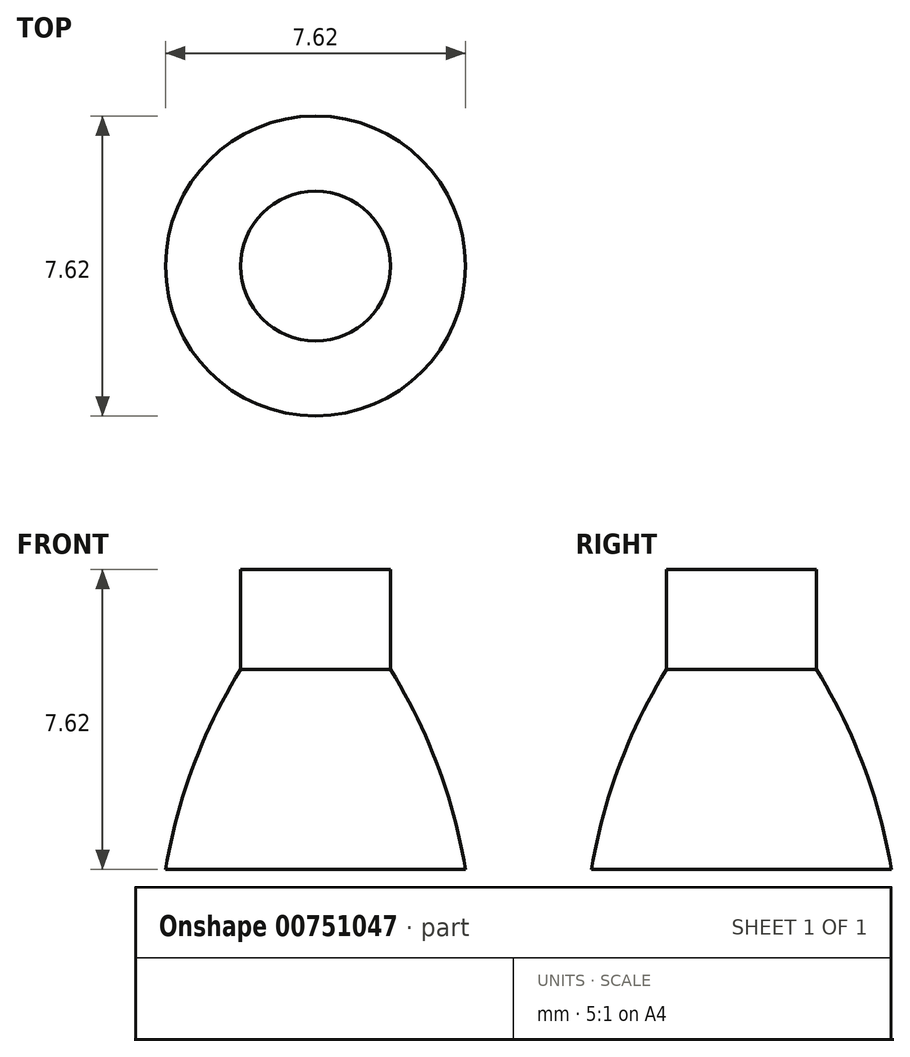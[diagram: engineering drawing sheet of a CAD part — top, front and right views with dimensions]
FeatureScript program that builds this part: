
annotation { "Feature Type Name" : "Feature", "Feature Type Description" : "" }
export const myFeature = defineFeature(function(context is Context, id is Id, definition is map)
    precondition{}
    {
        {
            var Q0;
            Q0=qCreatedBy(makeId("Front.planeOp"),FACE);
            var sketch = newSketch(context, id + "F0", { "sketchPlane" : qUnion([Q0])});
            skLineSegment(sketch, "E0", {"start": v(0, 0) * mm, "end": v(1.9, 0) * mm});
            skLineSegment(sketch, "E1", {"start": v(1.9, 0) * mm, "end": v(1.9, -2.54) * mm});
            skLineSegment(sketch, "E2", {"start": v(0, 0) * mm, "end": v(0, -7.62) * mm});
            skLineSegment(sketch, "E3", {"start": v(0, -7.62) * mm, "end": v(3.81, -7.62) * mm});
            skArc(sketch, "E4", {"start": v(3.81, -7.62) * mm, "mid": v(3.1, -4.99) * mm, "end": v(1.9, -2.54) * mm});
            skSolve(sketch);
        }
        {
            var Q0;
            Q0=makeQuery(id+"F0.imprint","IMPRINT",FACE,{"disambiguationData":[TD([[makeQuery(id+"F0.imprint","IMPRINT",EDGE,{"derivedFrom":sQuery(id+"F0.wireOp",EDGE,"E0")}),-1.0]])]});
            var Q1;
            Q1=sQuery(id+"F0.wireOp",EDGE,"E2");
            revolve(context, id + "F1", {"surfaceOperationType" : NewSurfaceOperationType.NEW, "entities" : qUnion([Q0]), "axis" : qUnion([Q1]), "revolveType" : RevolveType.FULL});
        }
    });
